FCSTD DOCUMENT  (FreeCAD 0.21R38887 (Git))
Label: ШВПY
License: All rights reserved
LicenseURL: http://en.wikipedia.org/wiki/All_rights_reserved
objects: Sketcher::SketchObject×3, Part::Helix×2, Part::Sweep×2, Part::Cut×2, PartDesign::Revolution×1, PartDesign::Body×1
note: 16 computed .brp shape members not serialized (recipe doc carries the construction recipe); baked Part::Feature solids carry a one-line shape summary decoded from their .brp
EXTERNAL_REF file=ТаблицаПараметров.FCStd obj=Spreadsheet006

FEATURE [Sketcher::SketchObject] Sketch
  ArcFitTolerance = 0
  ExternalBSplineMaxDegree = 0
  ExternalBSplineTolerance = 0
  FullyConstrained = true
  InternalTolerance = 1e-06
  InvalidShape = false
  MakeInternals = false
  MapMode = 3
  TreeRank = 11
  ValidateShape = false
  expr: Constraints[10] = <<ТаблицаПараметров>>#<<ШВП>>.lenY
  expr: Constraints[14] = <<ТаблицаПараметров>>#<<ШВП>>.lenY / 2 - <<ТаблицаПараметров>>#<<ШВП>>.lenMuftaY
  expr: Constraints[18] = <<ТаблицаПараметров>>#<<ШВП>>.diamMuftaY / 2
  expr: Constraints[24] = <<ТаблицаПараметров>>#<<ШВП>>.diamSrewY / 2
  expr: Constraints[27] = <<ТаблицаПараметров>>#<<ШВП>>.diamYval / 2
  expr: Constraints[28] = <<ТаблицаПараметров>>#<<ШВП>>.lenY / 2 - <<ТаблицаПараметров>>#<<ШВП>>.lenValY1
  sketch-geometry (10):
    g0: LineSegment StartX=0 StartY=-203.5 StartZ=0 EndX=0 EndY=203.5 EndZ=0
    g1: LineSegment StartX=0 StartY=-203.5 StartZ=0 EndX=-5 EndY=-203.5 EndZ=0
    g2: LineSegment StartX=-6 StartY=-202.5 StartZ=0 EndX=-6 EndY=-167.5 EndZ=0
    g3: LineSegment StartX=-6 StartY=-167.5 StartZ=0 EndX=-8 EndY=-167.5 EndZ=0
    g4: LineSegment StartX=-8 StartY=193.5 StartZ=0 EndX=-5 EndY=193.5 EndZ=0
    g5: LineSegment StartX=-4 StartY=203.5 StartZ=0 EndX=0 EndY=203.5 EndZ=0
    g6: LineSegment StartX=-6 StartY=-202.5 StartZ=0 EndX=-5 EndY=-203.5 EndZ=0
    g7: LineSegment StartX=-5 StartY=202.5 StartZ=0 EndX=-4 EndY=203.5 EndZ=0
    g8: LineSegment StartX=-5 StartY=193.5 StartZ=0 EndX=-5 EndY=202.5 EndZ=0
    g9: LineSegment StartX=-8 StartY=-167.5 StartZ=0 EndX=-8 EndY=193.5 EndZ=0
  constraints (29):
    c: Coincident(g1,g0)
    c: Vertical(g2)
    c: Coincident(g3,g2)
    c: Coincident(g5,g0)
    c: Horizontal(g1)
    c: Horizontal(g3)
    c: Horizontal(g4)
    c: Horizontal(g5)
    c: Coincident(g2,g6)
    c: Coincident(g1,g6)
    c: DistanceY(g0,g0) = 407
    c: PointOnObject(g0,g-2)
    c: Symmetric(g0,g0,g-1)
    c: Coincident(g7,g5)
    c: DistanceY(g-1,g4) = 193.5
    c: Coincident(g8,g4)
    c: Coincident(g8,g7)
    c: Vertical(g8)
    c: DistanceX(g7,g0) = 5
    c: Angle(g7) = 0.785398
    c: DistanceX(g7,g5) = 1
    c: Coincident(g9,g3)
    c: Coincident(g9,g4)
    c: Vertical(g9)
    c: DistanceX(g4,g-1) = 8
    c: Angle(g6) = -0.785398
    c: DistanceX(g2,g1) = 1
    c: DistanceX(g2,g-1) = 6
    c: DistanceY(g2,g-1) = 167.5
FEATURE [PartDesign::Revolution] Revolution
  AddSubType = 0
  Angle = 360
  Axis = (0,1,0)
  Base = (0,0,0)
  ClaimChildren = false
  Fit = 0
  FitJoin = 0
  InnerFit = 0
  InnerFitJoin = 0
  InvalidShape = false
  Linearize = true
  NewSolid = false
  Profile = -> Sketch
  ReferenceAxis = -> Sketch [V_Axis]
  Suppress = false
  TreeRank = 12
  ValidateShape = true
  _ProfileBasedVersion = 1
FEATURE [PartDesign::Body] Body
  AutoGroupSolids = false
  ClaimAllChildren = false
  ExportMode = 0
  Group = -> [Sketch,Revolution]
  InvalidShape = false
  Origin = -> Origin
  Tip = -> Revolution
  TreeRank = 10
  ValidateShape = false
  _ExportChildren = -> [Revolution]
  _GroupVersion = 1
FEATURE [Part::Helix] Helix  label="Гвинт"
  Angle = 0
  AttacherType = Attacher::AttachEngine3D
  Height = 363.5
  InvalidShape = false
  LocalCoord = 0
  Pitch = 5
  Placement = pos=(0,-167.5,0) rot=(0,0.707107,0.707107;3.14159rad)
  Radius = 8
  SegmentLength = 1
  Style = 1
  TreeRank = 15
  ValidateShape = false
  expr: Placement.Base.y = -(<<ТаблицаПараметров>>#<<ШВП>>.lenY / 2 - <<ТаблицаПараметров>>#<<ШВП>>.lenValY1)
  expr: Height = <<ТаблицаПараметров>>#<<ШВП>>.lenY - <<ТаблицаПараметров>>#<<ШВП>>.lenValY1 - <<ТаблицаПараметров>>#<<ШВП>>.lenMuftaY + <<ТаблицаПараметров>>#<<ШВП>>.ShagScrewY / 2
  expr: Pitch = <<ТаблицаПараметров>>#<<ШВП>>.ShagScrewY
  expr: Radius = <<ТаблицаПараметров>>#<<ШВП>>.diamSrewY / 2
FEATURE [Sketcher::SketchObject] Sketch001
  ArcFitTolerance = 0
  ExternalBSplineMaxDegree = 0
  ExternalBSplineTolerance = 0
  FullyConstrained = true
  InternalTolerance = 1e-06
  InvalidShape = false
  MakeInternals = false
  TreeRank = 14
  ValidateShape = false
  expr: Constraints[2] = <<ТаблицаПараметров>>#<<ШВП>>.lenY / 2 - <<ТаблицаПараметров>>#<<ШВП>>.lenValY1
  sketch-geometry (1):
    g0: Circle CenterX=-8 CenterY=-167.5 CenterZ=0 NormalX=0 NormalY=0 NormalZ=1 AngleXU=0 Radius=1.3
  constraints (3):
    c: DistanceX(g0,g-1) = 8
    c: Radius(g0) = 1.3
    c: DistanceY(g0,g-1) = 167.5
FEATURE [Part::Sweep] Sweep
  Frenet = true
  InvalidShape = false
  Linearize = true
  Sections = -> [Sketch001]
  Solid = true
  Spine = -> Helix
  Transition = 1
  TreeRank = 16
  ValidateShape = false
FEATURE [Part::Cut] Cut
  Base = -> Body
  InvalidShape = false
  Tool = -> Sweep
  TreeRank = 17
  ValidateShape = false
FEATURE [Part::Helix] Helix001  label="Гвинт001"
  Angle = 0
  AttacherType = Attacher::AttachEngine3D
  Height = 10
  InvalidShape = false
  LocalCoord = 0
  Pitch = 1
  Placement = pos=(0,-203.5,0) rot=(0,0.707107,0.707107;3.14159rad)
  Radius = 6
  SegmentLength = 1
  Style = 1
  TreeRank = 18
  ValidateShape = false
  expr: Placement.Base.y = -<<ТаблицаПараметров>>#<<ШВП>>.lenY / 2
FEATURE [Sketcher::SketchObject] Sketch002
  ArcFitTolerance = 0
  ExternalBSplineMaxDegree = 0
  ExternalBSplineTolerance = 0
  FullyConstrained = true
  InternalTolerance = 1e-06
  InvalidShape = false
  MakeInternals = false
  TreeRank = 19
  ValidateShape = false
  expr: Constraints[6] = 10.918 / 2
  expr: Constraints[7] = ТаблицаПараметров#<<ШВП>>.lenY / 2
  expr: Constraints[8] = ТаблицаПараметров#<<ШВП>>.diamYval / 2 + 1
  sketch-geometry (3):
    g0: LineSegment StartX=-7 StartY=-202.61 StartZ=0 EndX=-7 EndY=-204.39 EndZ=0
    g1: LineSegment StartX=-7 StartY=-204.39 StartZ=0 EndX=-5.459 EndY=-203.5 EndZ=0
    g2: LineSegment StartX=-5.459 StartY=-203.5 StartZ=0 EndX=-7 EndY=-202.61 EndZ=0
  constraints (9):
    c: Coincident(g2,g1)
    c: Coincident(g2,g0)
    c: Coincident(g0,g1)
    c: Angle(g2,g1) = 1.0472
    c: Vertical(g0)
    c: Angle(g0,g2) = 1.0472
    c: DistanceX(g1,g-1) = 5.459
    c: DistanceY(g1,g-1) = 203.5
    c: DistanceX(g0,g-1) = 7
FEATURE [Part::Sweep] Sweep001
  Frenet = true
  InvalidShape = false
  Linearize = true
  Sections = -> [Sketch002]
  Solid = true
  Spine = -> Helix001
  Transition = 1
  TreeRank = 20
  ValidateShape = false
FEATURE [Part::Cut] Cut001  label="ШВПY"
  Base = -> Cut
  InvalidShape = false
  Tool = -> Sweep001
  TreeRank = 21
  ValidateShape = false
